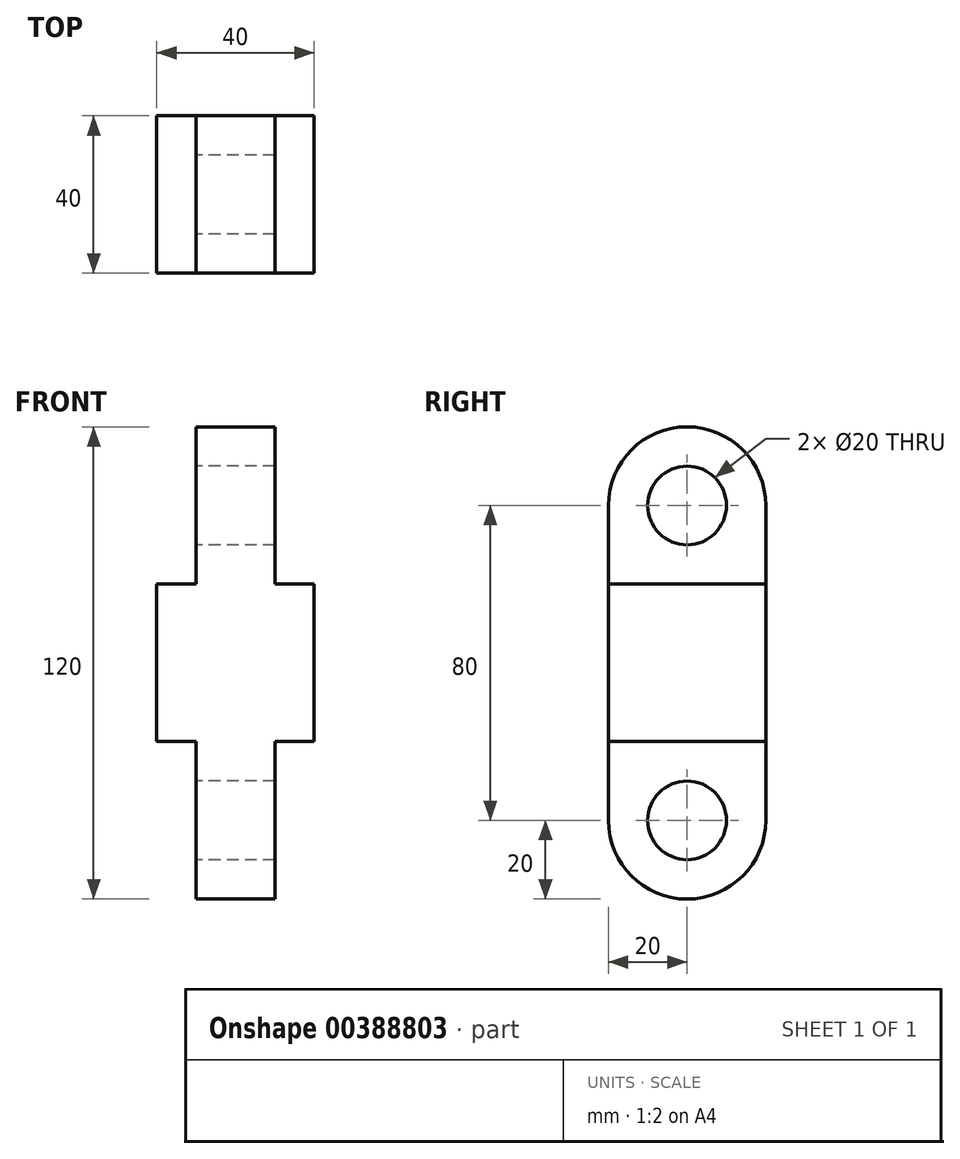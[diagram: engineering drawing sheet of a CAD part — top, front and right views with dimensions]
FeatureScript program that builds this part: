
annotation { "Feature Type Name" : "Feature", "Feature Type Description" : "" }
export const myFeature = defineFeature(function(context is Context, id is Id, definition is map)
    precondition{}
    {
        {
            var Q0;
            Q0=qCreatedBy(makeId("Right.planeOp"),FACE);
            var sketch = newSketch(context, id + "F0", { "sketchPlane" : qUnion([Q0])});
            skLineSegment(sketch, "E0.bottom", {"start": v(-20, 0) * mm, "end": v(20, 0) * mm});
            skLineSegment(sketch, "E0.top", {"start": v(0, 60) * mm, "end": v(0, 60) * mm});
            skLineSegment(sketch, "E0.left", {"start": v(-20, 0) * mm, "end": v(-20, 40) * mm});
            skLineSegment(sketch, "E0.right", {"start": v(20, 0) * mm, "end": v(20, 40) * mm});
            skLineSegment(sketch, "E1", {"start": v(0, 60) * mm, "end": v(0, 40) * mm, "construction": true});
            skPoint(sketch, "E1.endSnap0", {"position": v(0, 60) * mm});
            skCircle(sketch, "E2", {"center": v(0, 40) * mm, "radius": 10 * mm});
            skPoint(sketch, "E3.visualSharp", {"position": v(-20, 60) * mm});
            skArc(sketch, "E3.filletArc", {"start": v(0, 60) * mm, "mid": v(-14.14, 54.14) * mm, "end": v(-20, 40) * mm});
            skPoint(sketch, "E4.visualSharp", {"position": v(20, 60) * mm});
            skArc(sketch, "E4.filletArc", {"start": v(20, 40) * mm, "mid": v(14.14, 54.14) * mm, "end": v(0, 60) * mm});
            skSolve(sketch);
        }
        {
            var Q0;
            Q0 = qSketchRegion(id + "F0", true);
            extrude(context, id + "F1", {"entities" : qUnion([Q0]), "depth" : 10 * mm});
        }
        {
            var Q0;
            Q0=makeQuery(id+"F1.opExtrude","CAP_FACE",FACE,{"disambiguationData":[OSD([sQuery(id+"F0.wireOp",EDGE,"E0.bottom"),sQuery(id+"F0.wireOp",EDGE,"E0.left"),sQuery(id+"F0.wireOp",EDGE,"E0.right"),sQuery(id+"F0.wireOp",EDGE,"E2"),sQuery(id+"F0.wireOp",EDGE,"E3.filletArc"),sQuery(id+"F0.wireOp",EDGE,"E4.filletArc")])],"isStart":false});
            var sketch = newSketch(context, id + "F2", { "sketchPlane" : qUnion([Q0])});
            skLineSegment(sketch, "E5.bottom", {"start": v(-20, 0) * mm, "end": v(20, 0) * mm});
            skLineSegment(sketch, "E5.top", {"start": v(-20, 20) * mm, "end": v(20, 20) * mm});
            skLineSegment(sketch, "E5.left", {"start": v(-20, 0) * mm, "end": v(-20, 20) * mm});
            skLineSegment(sketch, "E5.right", {"start": v(20, 0) * mm, "end": v(20, 20) * mm});
            skSolve(sketch);
        }
        {
            var Q0;
            Q0 = qSketchRegion(id + "F2", true);
            extrude(context, id + "F3", {"entities" : qUnion([Q0]), "operationType" : NewBodyOperationType.ADD, "depth" : 10 * mm});
        }
        {
            var Q0;
            Q0=makeQuery(id+"F1.opExtrude","SWEPT_BODY",BODY,{"disambiguationData":[OSD([sQuery(id+"F0.wireOp",EDGE,"E0.bottom"),sQuery(id+"F0.wireOp",EDGE,"E0.left"),sQuery(id+"F0.wireOp",EDGE,"E0.right"),sQuery(id+"F0.wireOp",EDGE,"E2"),sQuery(id+"F0.wireOp",EDGE,"E3.filletArc"),sQuery(id+"F0.wireOp",EDGE,"E4.filletArc")])]});
            var Q1;
            Q1=qCreatedBy(makeId("Right.planeOp"),FACE);
            mirror(context, id + "F4", {"operationType" : NewBodyOperationType.ADD, "entities" : qUnion([Q0]), "mirrorPlane" : qUnion([Q1])});
        }
        {
            var Q0;
            Q0=makeQuery(id+"F1.opExtrude","SWEPT_BODY",BODY,{"disambiguationData":[OSD([sQuery(id+"F0.wireOp",EDGE,"E0.bottom"),sQuery(id+"F0.wireOp",EDGE,"E0.left"),sQuery(id+"F0.wireOp",EDGE,"E0.right"),sQuery(id+"F0.wireOp",EDGE,"E2"),sQuery(id+"F0.wireOp",EDGE,"E3.filletArc"),sQuery(id+"F0.wireOp",EDGE,"E4.filletArc")])]});
            var Q1;
            Q1=qCreatedBy(makeId("Top.planeOp"),FACE);
            mirror(context, id + "F5", {"operationType" : NewBodyOperationType.ADD, "entities" : qUnion([Q0]), "mirrorPlane" : qUnion([Q1])});
        }
    });
